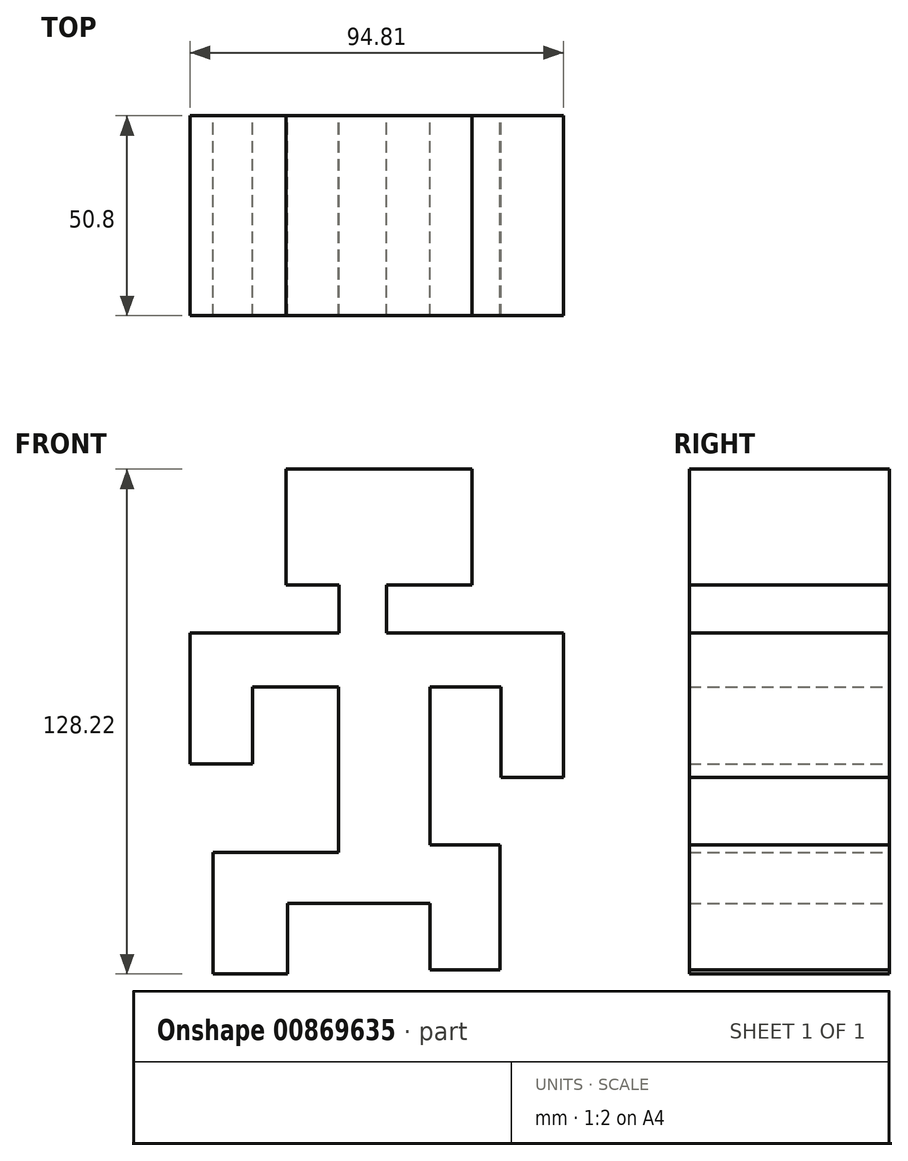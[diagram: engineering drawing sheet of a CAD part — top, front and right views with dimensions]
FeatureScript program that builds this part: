
annotation { "Feature Type Name" : "Feature", "Feature Type Description" : "" }
export const myFeature = defineFeature(function(context is Context, id is Id, definition is map)
    precondition{}
    {
        {
            var Q0;
            Q0=qCreatedBy(makeId("Front.planeOp"),FACE);
            var sketch = newSketch(context, id + "F0", { "sketchPlane" : qUnion([Q0])});
            skLineSegment(sketch, "E0.bottom", {"start": v(-19.42, 62.2) * mm, "end": v(27.88, 62.2) * mm});
            skLineSegment(sketch, "E0.top", {"start": v(-19.42, 32.8) * mm, "end": v(-5.94, 32.8) * mm});
            skLineSegment(sketch, "E0.left", {"start": v(-19.42, 62.2) * mm, "end": v(-19.42, 32.8) * mm});
            skLineSegment(sketch, "E0.right", {"start": v(27.88, 62.2) * mm, "end": v(27.88, 32.8) * mm});
            skLineSegment(sketch, "E1", {"start": v(-5.94, 32.8) * mm, "end": v(-5.94, 20.53) * mm});
            skLineSegment(sketch, "E2", {"start": v(-5.94, 20.53) * mm, "end": v(-43.78, 20.53) * mm});
            skLineSegment(sketch, "E3", {"start": v(-43.78, 20.53) * mm, "end": v(-43.78, -12.68) * mm});
            skLineSegment(sketch, "E4", {"start": v(-43.78, -12.68) * mm, "end": v(-27.88, -12.68) * mm});
            skLineSegment(sketch, "E5", {"start": v(-27.88, -12.68) * mm, "end": v(-27.88, 6.84) * mm});
            skLineSegment(sketch, "E6", {"start": v(-27.88, 6.84) * mm, "end": v(-6.14, 6.84) * mm});
            skLineSegment(sketch, "E7", {"start": v(-6.14, 6.84) * mm, "end": v(-6.14, -35.22) * mm});
            skLineSegment(sketch, "E8", {"start": v(-6.14, -35.22) * mm, "end": v(-37.94, -35.22) * mm});
            skLineSegment(sketch, "E9", {"start": v(-37.94, -35.22) * mm, "end": v(-37.94, -66.02) * mm});
            skLineSegment(sketch, "E10", {"start": v(-37.94, -66.02) * mm, "end": v(-19.02, -66.02) * mm});
            skLineSegment(sketch, "E11", {"start": v(-19.02, -66.02) * mm, "end": v(-19.02, -48.1) * mm});
            skLineSegment(sketch, "E12", {"start": v(-19.02, -48.1) * mm, "end": v(17.2, -48.1) * mm});
            skLineSegment(sketch, "E13", {"start": v(17.2, -48.1) * mm, "end": v(17.2, -65.01) * mm});
            skLineSegment(sketch, "E14", {"start": v(17.2, -65.01) * mm, "end": v(34.92, -65.01) * mm});
            skLineSegment(sketch, "E15", {"start": v(34.92, -65.01) * mm, "end": v(34.92, -33.21) * mm});
            skLineSegment(sketch, "E16", {"start": v(34.92, -33.21) * mm, "end": v(17.2, -33.21) * mm});
            skLineSegment(sketch, "E17", {"start": v(17.2, -33.21) * mm, "end": v(17.2, 6.84) * mm});
            skLineSegment(sketch, "E18", {"start": v(17.2, 6.84) * mm, "end": v(35.12, 6.84) * mm});
            skLineSegment(sketch, "E19", {"start": v(35.12, 6.84) * mm, "end": v(35.12, -16.1) * mm});
            skLineSegment(sketch, "E20", {"start": v(35.12, -16.1) * mm, "end": v(51.03, -16.1) * mm});
            skLineSegment(sketch, "E21", {"start": v(51.03, -16.1) * mm, "end": v(51.03, 20.53) * mm});
            skLineSegment(sketch, "E22", {"start": v(51.03, 20.53) * mm, "end": v(6.14, 20.53) * mm});
            skLineSegment(sketch, "E23", {"start": v(6.14, 20.53) * mm, "end": v(6.14, 32.8) * mm});
            skLineSegment(sketch, "E24.trimOffspring", {"start": v(6.14, 32.8) * mm, "end": v(27.88, 32.8) * mm});
            skSolve(sketch);
        }
        {
            var Q0;
            Q0 = qSketchRegion(id + "F0", true);
            extrude(context, id + "F1", {"entities" : qUnion([Q0]), "depth" : 50.8 * mm, "offsetDistance" : 25.4 * mm});
        }
    });
